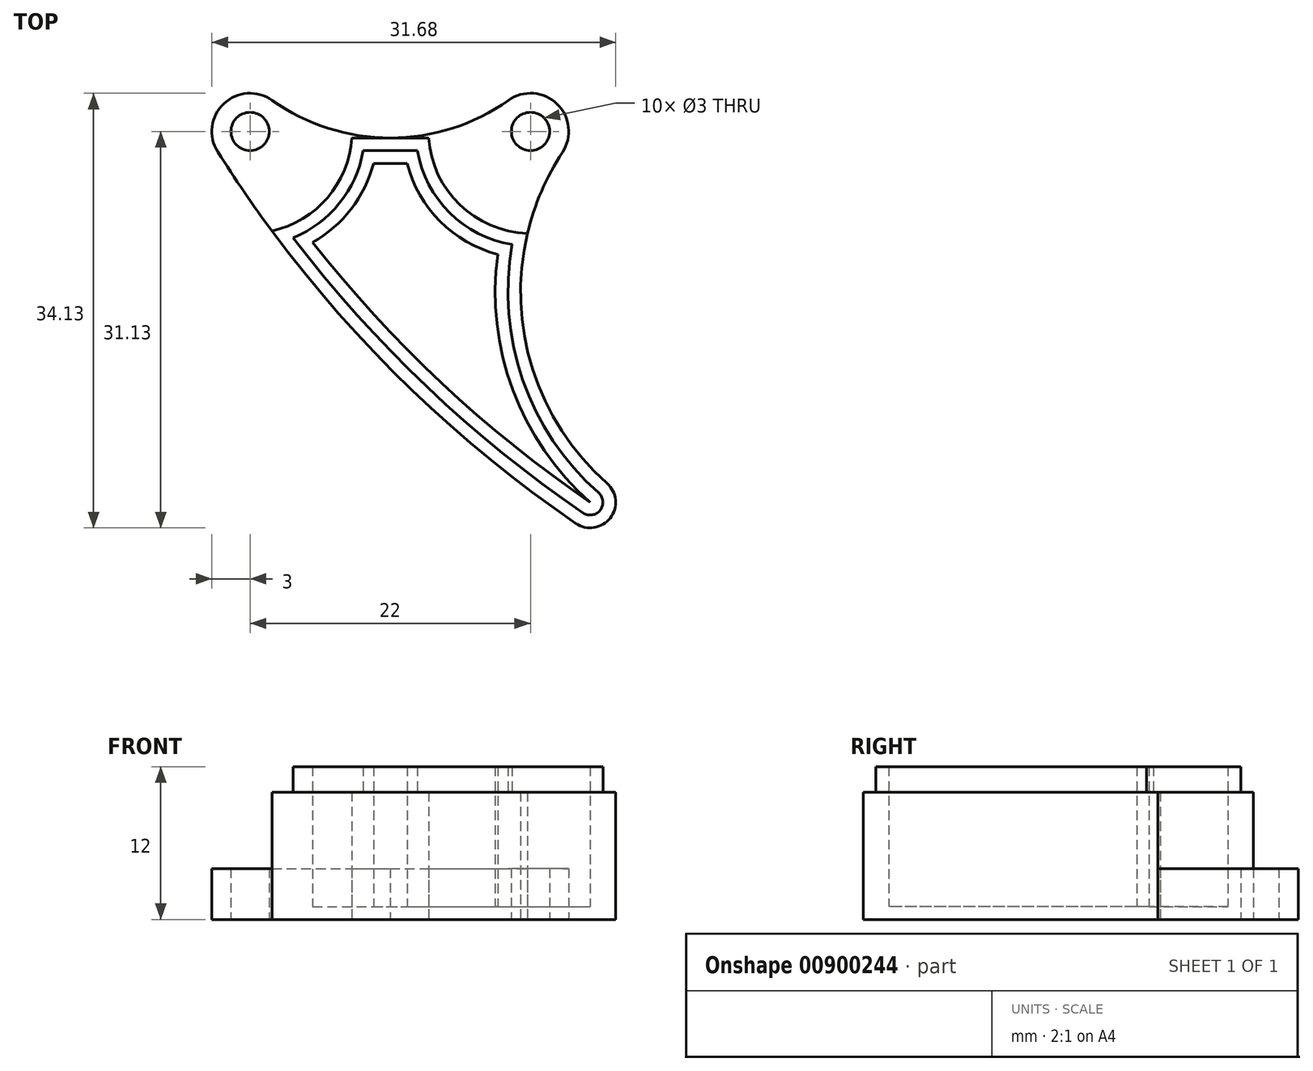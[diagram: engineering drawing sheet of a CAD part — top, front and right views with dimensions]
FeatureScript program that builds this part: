
annotation { "Feature Type Name" : "Feature", "Feature Type Description" : "" }
export const myFeature = defineFeature(function(context is Context, id is Id, definition is map)
    precondition{}
    {
        {
            var Q0;
            Q0=qCreatedBy(makeId("Top.planeOp"),FACE);
            var sketch = newSketch(context, id + "F0", { "sketchPlane" : qUnion([Q0])});
            skCircle(sketch, "E0", {"center": v(0, 0) * mm, "radius": 1.5 * mm});
            skCircle(sketch, "E1", {"center": v(-22, 0) * mm, "radius": 1.5 * mm});
            skArc(sketch, "E2", {"start": v(-20.26, 2.45) * mm, "mid": v(-24.06, 2.18) * mm, "end": v(-24.54, -1.6) * mm});
            skArc(sketch, "E3", {"start": v(2.5, -1.65) * mm, "mid": v(2.08, 2.16) * mm, "end": v(-1.74, 2.45) * mm});
            skArc(sketch, "E4", {"start": v(-20.26, 2.45) * mm, "mid": v(-11, -0.5) * mm, "end": v(-1.74, 2.45) * mm});
            skPoint(sketch, "E5.orphan", {"position": v(0, 3.87) * mm});
            skArc(sketch, "E6", {"start": v(3.55, -30.78) * mm, "mid": v(6.26, -30.35) * mm, "end": v(6, -27.63) * mm});
            skArc(sketch, "E7", {"start": v(2.5, -1.65) * mm, "mid": v(-0.6, -15.29) * mm, "end": v(6, -27.63) * mm});
            skArc(sketch, "E8", {"start": v(-24.54, -1.6) * mm, "mid": v(-11.99, -17.62) * mm, "end": v(3.55, -30.78) * mm});
            skArc(sketch, "E9", {"start": v(-20.28, -7.81) * mm, "mid": v(-15.93, -5.2) * mm, "end": v(-14.02, -0.5) * mm});
            skArc(sketch, "E10", {"start": v(-7.98, -0.5) * mm, "mid": v(-5.56, -5.75) * mm, "end": v(-0.23, -8) * mm});
            skLineSegment(sketch, "E11", {"start": v(-14.02, -0.5) * mm, "end": v(-7.98, -0.5) * mm});
            skLineSegment(sketch, "E12.0", {"start": v(-13.13, -1.5) * mm, "end": v(-8.87, -1.5) * mm});
            skArc(sketch, "E13.0", {"start": v(-8.87, -1.5) * mm, "mid": v(-6.34, -6.39) * mm, "end": v(-1.44, -8.88) * mm});
            skArc(sketch, "E14", {"start": v(4.12, -29.95) * mm, "mid": v(5.47, -29.74) * mm, "end": v(5.34, -28.38) * mm});
            skArc(sketch, "E15.trimOffspring", {"start": v(-18.63, -8.35) * mm, "mid": v(-14.99, -5.64) * mm, "end": v(-13.13, -1.5) * mm});
            skArc(sketch, "E16.0", {"start": v(-9.68, -2.5) * mm, "mid": v(-7.1, -7.05) * mm, "end": v(-2.57, -9.66) * mm});
            skLineSegment(sketch, "E16.1", {"start": v(-12.32, -2.5) * mm, "end": v(-9.68, -2.5) * mm});
            skArc(sketch, "E17.0", {"start": v(-23.7, -1.07) * mm, "mid": v(-23.08, -2.02) * mm, "end": v(-22.47, -2.96) * mm, "construction": true});
            skArc(sketch, "E18.trimOffspring", {"start": v(-18.63, -8.35) * mm, "mid": v(-8.12, -20.06) * mm, "end": v(4.12, -29.95) * mm});
            skArc(sketch, "E19.0", {"start": v(1.67, -1.1) * mm, "mid": v(1.1, -2) * mm, "end": v(0.6, -2.94) * mm, "construction": true});
            skArc(sketch, "E20.trimOffspring", {"start": v(-1.44, -8.88) * mm, "mid": v(-0.6, -19.52) * mm, "end": v(5.34, -28.38) * mm});
            skArc(sketch, "E21.0", {"start": v(-2.57, -9.66) * mm, "mid": v(-1.39, -20.3) * mm, "end": v(4.68, -29.13) * mm});
            skArc(sketch, "E22.0", {"start": v(-17.84, -7.74) * mm, "mid": v(-17.77, -7.83) * mm, "end": v(-17.7, -7.91) * mm, "construction": true});
            skArc(sketch, "E23.0", {"start": v(-18.26, -9.27) * mm, "mid": v(-18.13, -9.22) * mm, "end": v(-18, -9.17) * mm, "construction": true});
            skArc(sketch, "E24.trimOffspring", {"start": v(-17.09, -8.71) * mm, "mid": v(-6.98, -19.75) * mm, "end": v(4.68, -29.13) * mm});
            skArc(sketch, "E25.trimOffspring", {"start": v(-17.09, -8.71) * mm, "mid": v(-14.07, -6.1) * mm, "end": v(-12.32, -2.5) * mm});
            skSolve(sketch);
        }
        {
            var Q0;
            Q0=makeQuery(id+"F0.imprint","IMPRINT",FACE,{"disambiguationData":[TD([[makeQuery(id+"F0.imprint","IMPRINT",EDGE,{"derivedFrom":sQuery(id+"F0.wireOp",EDGE,"E1")}),-1.0]])]});
            var Q1;
            Q1=makeQuery(id+"F0.imprint","IMPRINT",FACE,{"disambiguationData":[TD([[makeQuery(id+"F0.imprint","IMPRINT",EDGE,{"derivedFrom":sQuery(id+"F0.wireOp",EDGE,"E0")}),-1.0]])]});
            extrude(context, id + "F1", {"entities" : qUnion([Q0, Q1]), "depth" : 4 * mm, "offsetDistance" : 25 * mm});
        }
        {
            var Q0;
            {var subQ4=sQuery(id+"F0.wireOp",EDGE,"E6");Q0=makeQuery(id+"F0.imprint","IMPRINT",FACE,{"disambiguationData":[TD([[makeQuery(id+"F0.imprint","IMPRINT",EDGE,{"derivedFrom":subQ4}),1.0]])]});}
            extrude(context, id + "F2", {"entities" : qUnion([Q0]), "depth" : 10 * mm, "offsetDistance" : 25 * mm});
        }
        {
            var Q0;
            Q0=makeQuery(id+"F0.imprint","IMPRINT",FACE,{"disambiguationData":[TD([[makeQuery(id+"F0.imprint","IMPRINT",EDGE,{"derivedFrom":sQuery(id+"F0.wireOp",EDGE,"E12.0")}),-1.0]])]});
            extrude(context, id + "F3", {"entities" : qUnion([Q0]), "operationType" : NewBodyOperationType.ADD, "depth" : 12 * mm, "offsetDistance" : 25 * mm});
        }
        {
            var Q0;
            Q0=makeQuery(id+"F0.imprint","IMPRINT",FACE,{"disambiguationData":[TD([[makeQuery(id+"F0.imprint","IMPRINT",EDGE,{"derivedFrom":sQuery(id+"F0.wireOp",EDGE,"E16.0")}),-1.0]])]});
            extrude(context, id + "F4", {"entities" : qUnion([Q0]), "operationType" : NewBodyOperationType.ADD, "depth" : 1 * mm, "offsetDistance" : 25 * mm});
        }
    });
